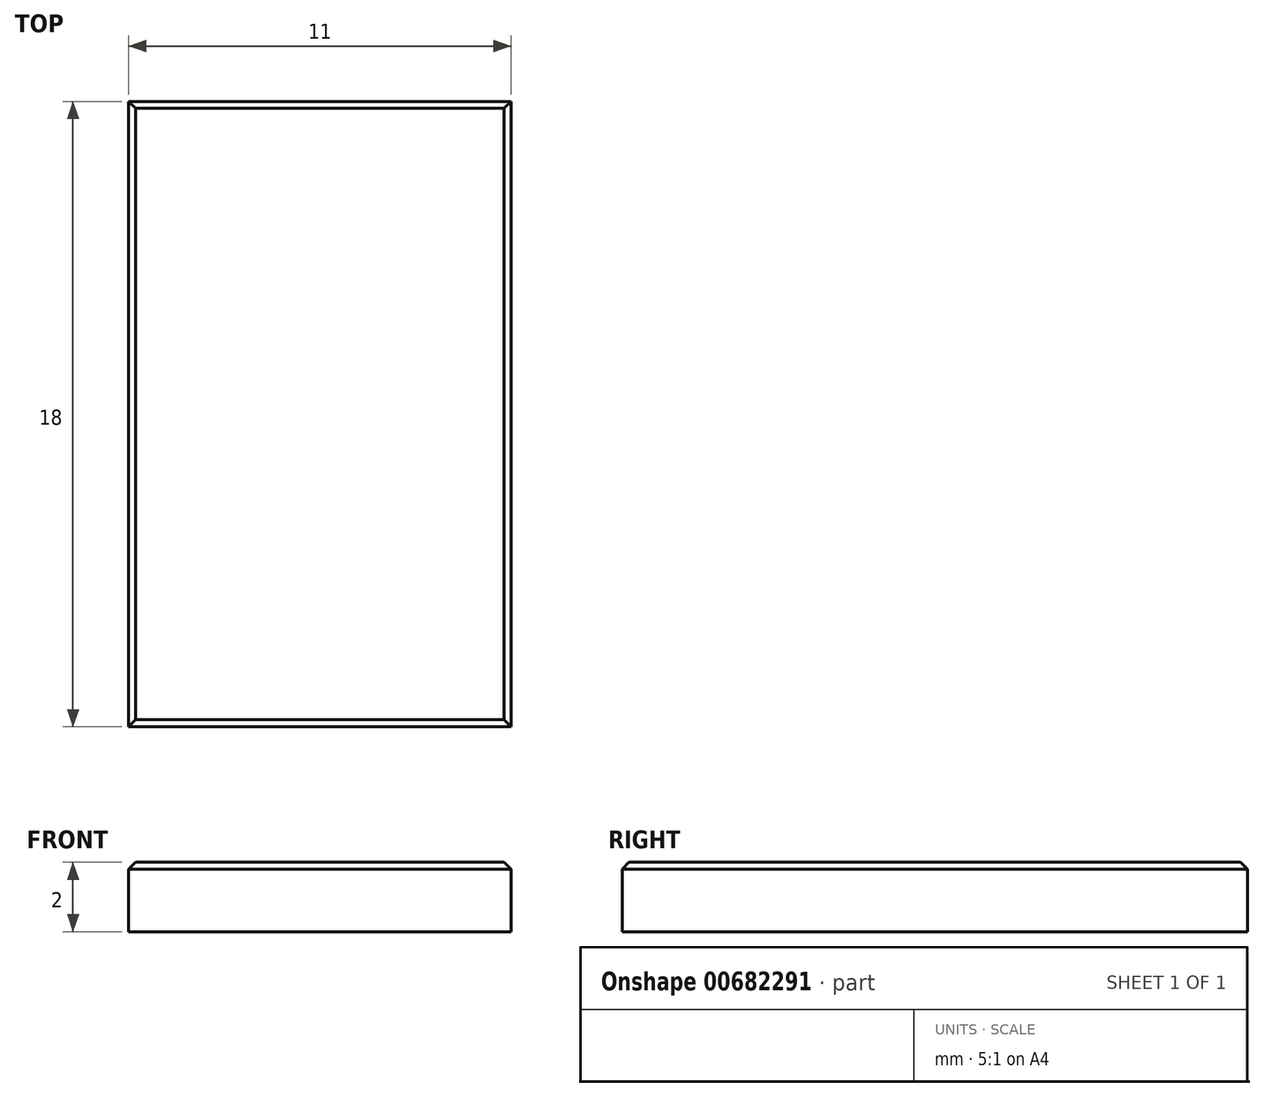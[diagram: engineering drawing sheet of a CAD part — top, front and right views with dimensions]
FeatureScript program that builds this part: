
annotation { "Feature Type Name" : "Feature", "Feature Type Description" : "" }
export const myFeature = defineFeature(function(context is Context, id is Id, definition is map)
    precondition{}
    {
        {
            var Q0;
            Q0=qCreatedBy(makeId("Top.planeOp"),FACE);
            var sketch = newSketch(context, id + "F0", { "sketchPlane" : qUnion([Q0])});
            skLineSegment(sketch, "E0.bottom", {"start": v(-5.5, 9) * mm, "end": v(5.5, 9) * mm});
            skLineSegment(sketch, "E0.top", {"start": v(-5.5, -9) * mm, "end": v(5.5, -9) * mm});
            skLineSegment(sketch, "E0.left", {"start": v(-5.5, 9) * mm, "end": v(-5.5, -9) * mm});
            skLineSegment(sketch, "E0.right", {"start": v(5.5, 9) * mm, "end": v(5.5, -9) * mm});
            skPoint(sketch, "E0.middle", {"position": v(0, 0) * mm});
            skSolve(sketch);
        }
        {
            var Q0;
            Q0=qSketchRegion(id+"F0",true);
            extrude(context, id + "F1", {"entities" : qUnion([Q0]), "depth" : 2 * mm, "offsetDistance" : 25 * mm});
        }
        {
            var Q0;
            Q0=makeQuery(id+"F1.opExtrude","CAP_EDGE",EDGE,{"disambiguationData":[OSD([sQuery(id+"F0.wireOp",EDGE,"E0.right")])],"isStart":false});
            var Q1;
            Q1=makeQuery(id+"F1.opExtrude","CAP_EDGE",EDGE,{"disambiguationData":[OSD([sQuery(id+"F0.wireOp",EDGE,"E0.top")])],"isStart":false});
            var Q2;
            Q2=makeQuery(id+"F1.opExtrude","CAP_EDGE",EDGE,{"disambiguationData":[OSD([sQuery(id+"F0.wireOp",EDGE,"E0.left")])],"isStart":false});
            var Q3;
            Q3=makeQuery(id+"F1.opExtrude","CAP_EDGE",EDGE,{"disambiguationData":[OSD([sQuery(id+"F0.wireOp",EDGE,"E0.bottom")])],"isStart":false});
            chamfer(context, id + "F2", {"entities" : qUnion([Q0, Q1, Q2, Q3]), "width" : .2 * mm, "tangentPropagation" : true});
        }
    });
